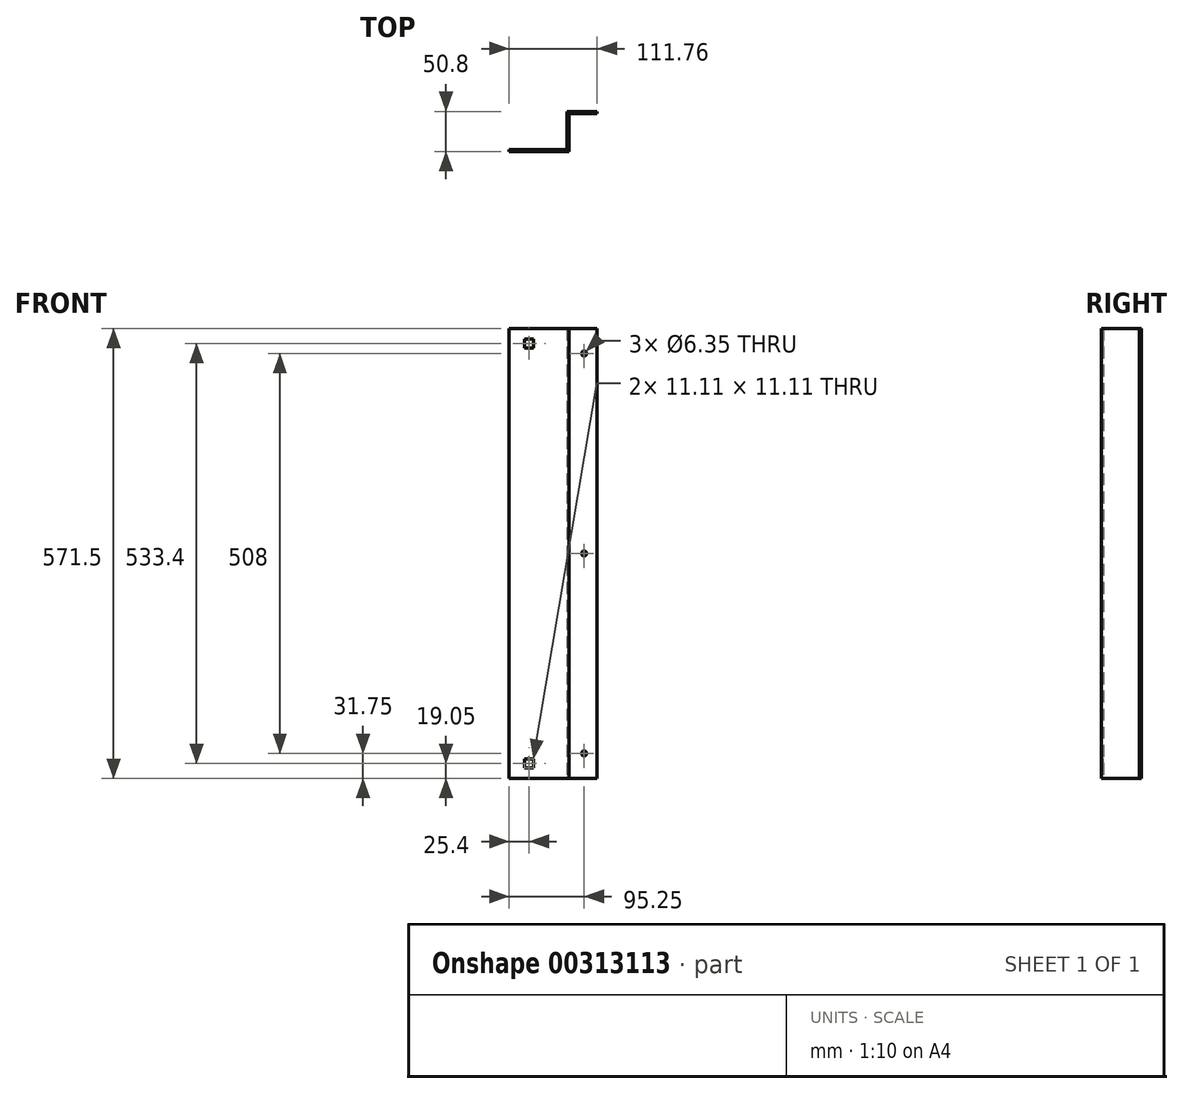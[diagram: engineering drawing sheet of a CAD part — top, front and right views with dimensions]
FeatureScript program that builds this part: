
annotation { "Feature Type Name" : "Feature", "Feature Type Description" : "" }
export const myFeature = defineFeature(function(context is Context, id is Id, definition is map)
    precondition{}
    {
        {
            var Q0;
            Q0=qCreatedBy(makeId("Top.planeOp"),FACE);
            var sketch = newSketch(context, id + "F0", { "sketchPlane" : qUnion([Q0])});
            skLineSegment(sketch, "E0", {"start": v(-2.54, 2.54) * mm, "end": v(-2.54, 50.8) * mm});
            skLineSegment(sketch, "E1", {"start": v(-2.54, 50.8) * mm, "end": v(35.56, 50.8) * mm});
            skLineSegment(sketch, "E2", {"start": v(35.56, 50.8) * mm, "end": v(35.56, 48.26) * mm});
            skLineSegment(sketch, "E3", {"start": v(35.56, 48.26) * mm, "end": v(0, 48.26) * mm});
            skLineSegment(sketch, "E4", {"start": v(0, 48.26) * mm, "end": v(0, 0) * mm});
            skLineSegment(sketch, "E5", {"start": v(-2.54, 2.54) * mm, "end": v(-76.2, 2.54) * mm});
            skLineSegment(sketch, "E6", {"start": v(-76.2, 2.54) * mm, "end": v(-76.2, 0) * mm});
            skLineSegment(sketch, "E7", {"start": v(-76.2, 0) * mm, "end": v(0, 0) * mm});
            skSolve(sketch);
        }
        {
            var Q0;
            Q0 = qSketchRegion(id + "F0", true);
            extrude(context, id + "F1", {"entities" : qUnion([Q0]), "endBound" : BoundingType.SYMMETRIC, "depth" : 571.5 * mm});
        }
        {
            var Q0;
            Q0=makeQuery(id+"F1.opExtrude","SWEPT_FACE",FACE,{"disambiguationData":[OSD([sQuery(id+"F0.wireOp",EDGE,"E7")])]});
            var sketch = newSketch(context, id + "F2", { "sketchPlane" : qUnion([Q0])});
            skLineSegment(sketch, "E8.bottom", {"start": v(-45.24, 261.14) * mm, "end": v(-56.36, 261.14) * mm});
            skLineSegment(sketch, "E8.top", {"start": v(-45.24, 272.26) * mm, "end": v(-56.36, 272.26) * mm});
            skLineSegment(sketch, "E8.left", {"start": v(-45.24, 261.14) * mm, "end": v(-45.24, 272.26) * mm});
            skLineSegment(sketch, "E8.right", {"start": v(-56.36, 261.14) * mm, "end": v(-56.36, 272.26) * mm});
            skPoint(sketch, "E8.middle", {"position": v(-50.8, 266.7) * mm});
            skLineSegment(sketch, "E9.bottom", {"start": v(-45.24, -272.26) * mm, "end": v(-56.36, -272.26) * mm});
            skLineSegment(sketch, "E9.top", {"start": v(-45.24, -261.14) * mm, "end": v(-56.36, -261.14) * mm});
            skLineSegment(sketch, "E9.left", {"start": v(-45.24, -272.26) * mm, "end": v(-45.24, -261.14) * mm});
            skLineSegment(sketch, "E9.right", {"start": v(-56.36, -272.26) * mm, "end": v(-56.36, -261.14) * mm});
            skPoint(sketch, "E9.middle", {"position": v(-50.8, -266.7) * mm});
            skCircle(sketch, "E10", {"center": v(19.05, 254) * mm, "radius": 3.18 * mm});
            skCircle(sketch, "E11", {"center": v(19.05, 0) * mm, "radius": 3.18 * mm});
            skLineSegment(sketch, "E12", {"start": v(-50.8, -266.7) * mm, "end": v(-50.8, 266.7) * mm, "construction": true});
            skPoint(sketch, "E13", {"position": v(-50.8, 0) * mm});
            skCircle(sketch, "E14", {"center": v(19.05, -254) * mm, "radius": 3.18 * mm});
            skSolve(sketch);
        }
        {
            var Q0;
            Q0 = qSketchRegion(id + "F2", true);
            extrude(context, id + "F3", {"entities" : qUnion([Q0]), "operationType" : NewBodyOperationType.REMOVE, "endBound" : BoundingType.THROUGH_ALL, "oppositeDirection" : true, "depth" : 25.4 * mm});
        }
    });
